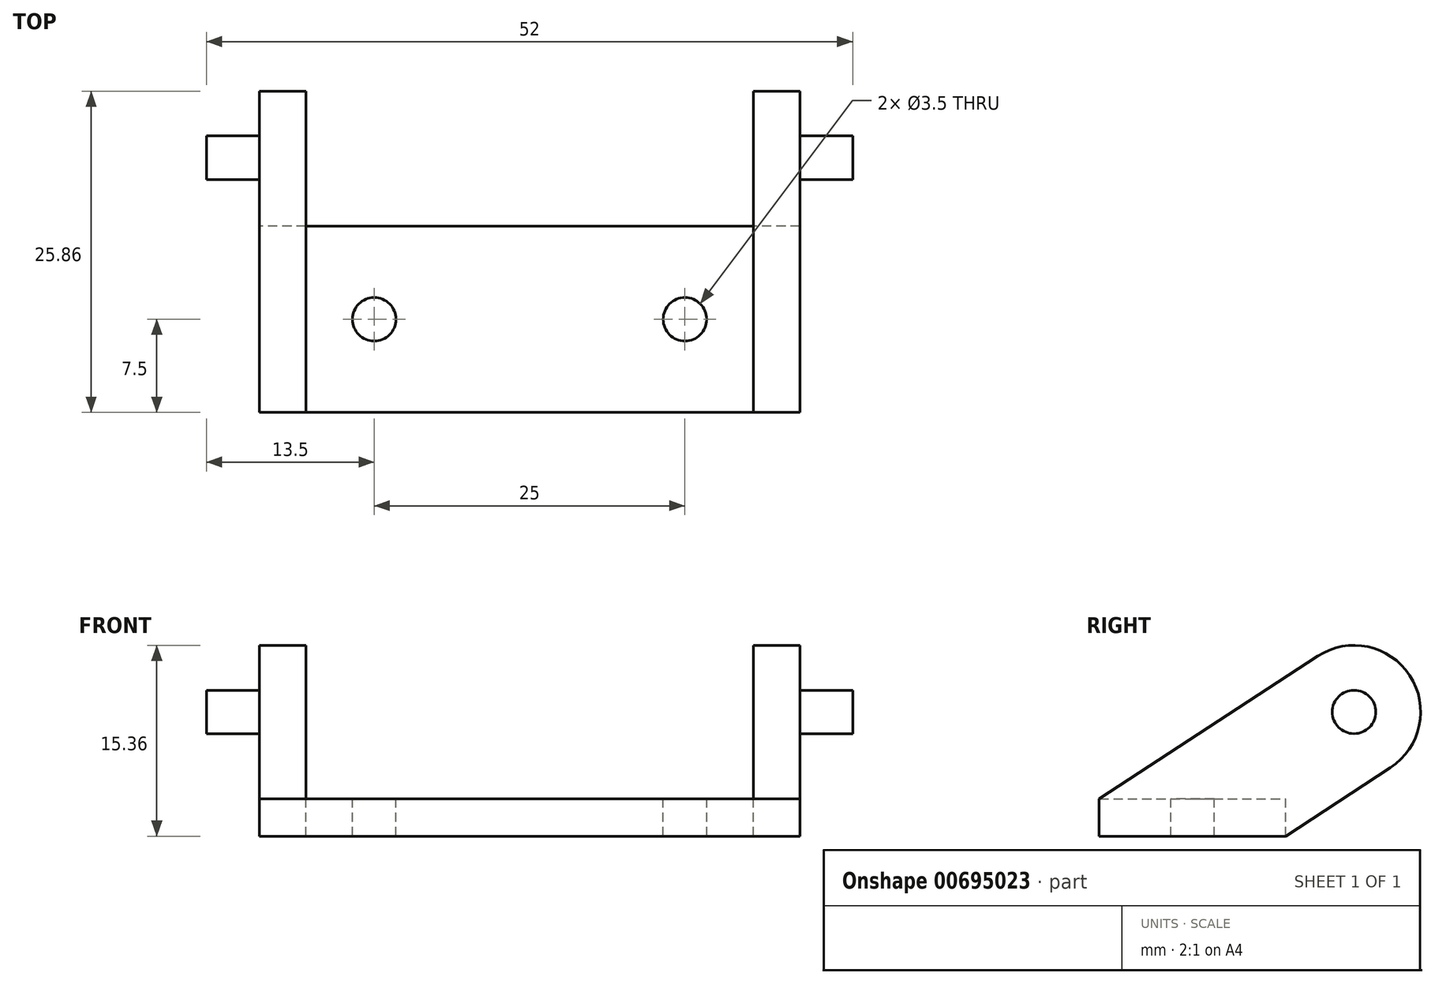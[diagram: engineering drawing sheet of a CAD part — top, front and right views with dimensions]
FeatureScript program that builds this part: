
annotation { "Feature Type Name" : "Feature", "Feature Type Description" : "" }
export const myFeature = defineFeature(function(context is Context, id is Id, definition is map)
    precondition{}
    {
        {
            var Q0;
            Q0=qCreatedBy(makeId("Right.planeOp"),FACE);
            var sketch = newSketch(context, id + "F0", { "sketchPlane" : qUnion([Q0])});
            skArc(sketch, "E0", {"start": v(23.43, 5.51) * mm, "mid": v(24.99, 12.93) * mm, "end": v(17.57, 14.49) * mm});
            skCircle(sketch, "E1", {"center": v(20.5, 10) * mm, "radius": 1.75 * mm});
            skLineSegment(sketch, "E2.bottom", {"start": v(0, 0) * mm, "end": v(15, 0) * mm});
            skLineSegment(sketch, "E2.top", {"start": v(0, 3) * mm, "end": v(15, 3) * mm});
            skLineSegment(sketch, "E2.left", {"start": v(0, 0) * mm, "end": v(0, 3) * mm});
            skLineSegment(sketch, "E2.right", {"start": v(15, 0) * mm, "end": v(15, 3) * mm});
            skLineSegment(sketch, "E3", {"start": v(0, 3) * mm, "end": v(17.57, 14.49) * mm});
            skLineSegment(sketch, "E4", {"start": v(15, 0) * mm, "end": v(23.43, 5.51) * mm});
            skSolve(sketch);
        }
        {
            var Q0;
            Q0=makeQuery(id+"F0.imprint","IMPRINT",FACE,{"disambiguationData":[TD([[makeQuery(id+"F0.imprint","IMPRINT",EDGE,{"derivedFrom":sQuery(id+"F0.wireOp",EDGE,"WoEYFcgc-MQ6B-Gypt-Egv2-rzsU5WrDNNNz.bottom")}),-1.0]])]});
            var Q1;
            Q1=makeQuery(id+"F0.imprint","IMPRINT",FACE,{"disambiguationData":[TD([[makeQuery(id+"F0.imprint","IMPRINT",EDGE,{"derivedFrom":sQuery(id+"F0.wireOp",EDGE,"WoEYFcgc-MQ6B-Gypt-Egv2-rzsU5WrDNNNz.bottom")}),1.0]])]});
            var Q2;
            Q2=makeQuery(id+"F0.imprint","IMPRINT",FACE,{"disambiguationData":[TD([[makeQuery(id+"F0.imprint","IMPRINT",EDGE,{"derivedFrom":sQuery(id+"F0.wireOp",EDGE,"E1")}),-1.0]])]});
            var Q3;
            Q3=makeQuery(id+"F0.imprint","IMPRINT",FACE,{"disambiguationData":[TD([[makeQuery(id+"F0.imprint","IMPRINT",EDGE,{"derivedFrom":sQuery(id+"F0.wireOp",EDGE,"E2.top")}),1.0]])]});
            var Q4;
            Q4=makeQuery(id+"F0.imprint","IMPRINT",FACE,{"disambiguationData":[TD([[makeQuery(id+"F0.imprint","IMPRINT",EDGE,{"derivedFrom":sQuery(id+"F0.wireOp",EDGE,"E2.bottom")}),1.0]])]});
            var Q5;
            Q5=sQuery(id+"F0.wireOp",EDGE,"WoEYFcgc-MQ6B-Gypt-Egv2-rzsU5WrDNNNz.top");
            var Q6;
            Q6=sQuery(id+"F0.wireOp",EDGE,"WoEYFcgc-MQ6B-Gypt-Egv2-rzsU5WrDNNNz.bottom");
            var Q7;
            Q7=sQuery(id+"F0.wireOp",EDGE,"WoEYFcgc-MQ6B-Gypt-Egv2-rzsU5WrDNNNz.left");
            var Q8;
            Q8=sQuery(id+"F0.wireOp",EDGE,"WoEYFcgc-MQ6B-Gypt-Egv2-rzsU5WrDNNNz.right");
            extrude(context, id + "F1", {"entities" : qUnion([Q0, Q1, Q2, Q3, Q4]), "surfaceEntities" : qUnion([Q5, Q6, Q7, Q8]), "depth" : 43.5 * mm, "offsetDistance" : 25 * mm, "symmetric" : true});
        }
        {
            var Q0;
            Q0=makeQuery(id+"F0.imprint","IMPRINT",FACE,{"disambiguationData":[TD([[makeQuery(id+"F0.imprint","IMPRINT",EDGE,{"derivedFrom":sQuery(id+"F0.wireOp",EDGE,"E1")}),1.0]])]});
            extrude(context, id + "F2", {"entities" : qUnion([Q0]), "operationType" : NewBodyOperationType.ADD, "depth" : 52 * mm, "offsetDistance" : 25 * mm, "symmetric" : true});
        }
        {
            var Q0;
            Q0=makeQuery(id+"F0.imprint","IMPRINT",FACE,{"disambiguationData":[TD([[makeQuery(id+"F0.imprint","IMPRINT",EDGE,{"derivedFrom":sQuery(id+"F0.wireOp",EDGE,"E1")}),1.0]])]});
            var Q1;
            Q1=makeQuery(id+"F0.imprint","IMPRINT",FACE,{"disambiguationData":[TD([[makeQuery(id+"F0.imprint","IMPRINT",EDGE,{"derivedFrom":sQuery(id+"F0.wireOp",EDGE,"E1")}),-1.0]])]});
            var Q2;
            Q2=makeQuery(id+"F0.imprint","IMPRINT",FACE,{"disambiguationData":[TD([[makeQuery(id+"F0.imprint","IMPRINT",EDGE,{"derivedFrom":sQuery(id+"F0.wireOp",EDGE,"WoEYFcgc-MQ6B-Gypt-Egv2-rzsU5WrDNNNz.bottom")}),1.0]])]});
            var Q3;
            Q3=makeQuery(id+"F0.imprint","IMPRINT",FACE,{"disambiguationData":[TD([[makeQuery(id+"F0.imprint","IMPRINT",EDGE,{"derivedFrom":sQuery(id+"F0.wireOp",EDGE,"E2.top")}),1.0]])]});
            extrude(context, id + "F3", {"entities" : qUnion([Q0, Q1, Q2, Q3]), "operationType" : NewBodyOperationType.REMOVE, "flatOperationType" : FlatOperationType.REMOVE, "oppositeDirection" : true, "depth" : 36 * mm, "offsetDistance" : 25 * mm, "domain" : OperationDomain.MODEL, "symmetric" : true});
        }
        {
            var Q0;
            Q0=makeQuery(id+"F3.boolean.opBoolean","COPY",FACE,{"derivedFrom":makeQuery(id+"F3.opExtrude","SWEPT_FACE",FACE,{"disambiguationData":[OSD([sQuery(id+"F0.wireOp",EDGE,"E2.top")])]})});
            var sketch = newSketch(context, id + "F4", { "sketchPlane" : qUnion([Q0])});
            skPoint(sketch, "E5", {"position": v(12.5, 7.5) * mm});
            skPoint(sketch, "E6.MirrorP", {"position": v(-12.5, 7.5) * mm});
            skLineSegment(sketch, "E7", {"start": v(12.5, 15) * mm, "end": v(12.5, 0) * mm});
            skSolve(sketch);
        }
        {
            var Q0;
            Q0=sQuery(id+"F4.wireOp",VERTEX,"E5");
            var Q1;
            Q1=sQuery(id+"F4.wireOp",VERTEX,"E6.MirrorP");
            var Q2;
            Q2=makeQuery(id+"F1.opExtrude","SWEPT_BODY",BODY,{"disambiguationData":[OSD([sQuery(id+"F0.wireOp",EDGE,"E0"),sQuery(id+"F0.wireOp",EDGE,"E1"),sQuery(id+"F0.wireOp",EDGE,"E2.bottom"),sQuery(id+"F0.wireOp",EDGE,"E2.left"),sQuery(id+"F0.wireOp",EDGE,"E3"),sQuery(id+"F0.wireOp",EDGE,"E4")])]});
            hole(context, id + "F5", {"style" : HoleStyle.SIMPLE, "endStyle" : HoleEndStyle.THROUGH, "holeDiameter" : 3.5 * mm, "majorDiameter" : 5 * mm, "isTappedThrough" : true, "tappedDepth" : 12 * mm, "tapClearance" : 3, "locations" : qUnion([Q0, Q1]), "scope" : qUnion([Q2])});
        }
    });
